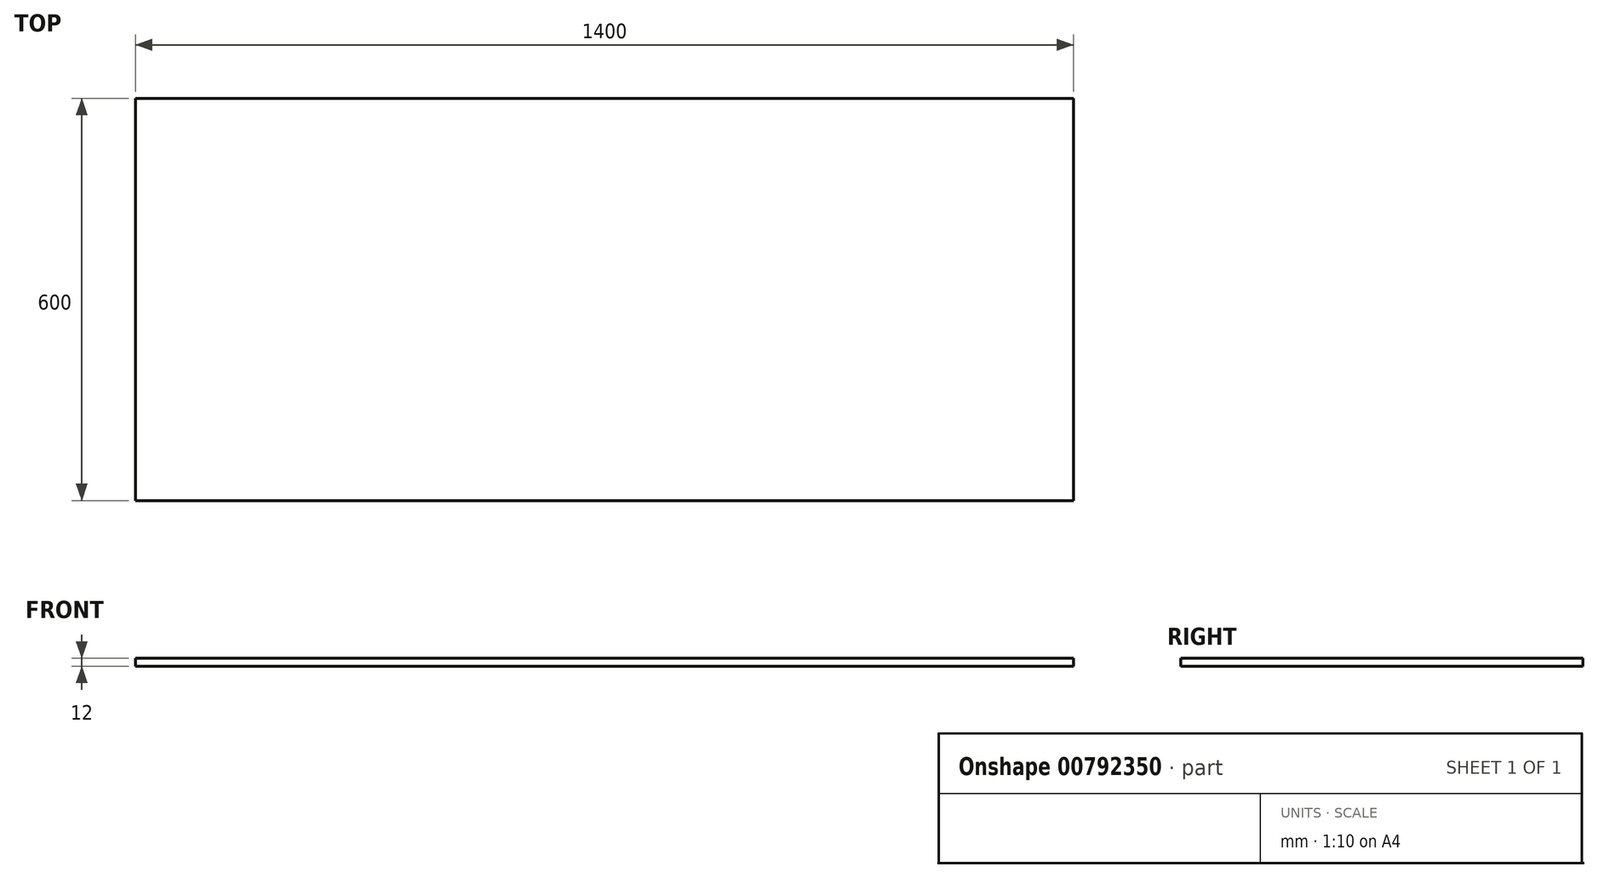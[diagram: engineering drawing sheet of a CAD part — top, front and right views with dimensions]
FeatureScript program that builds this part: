
annotation { "Feature Type Name" : "Feature", "Feature Type Description" : "" }
export const myFeature = defineFeature(function(context is Context, id is Id, definition is map)
    precondition{}
    {
        {
            var Q0;
            Q0=qCreatedBy(makeId("Top.planeOp"),FACE);
            var sketch = newSketch(context, id + "F0", { "sketchPlane" : qUnion([Q0])});
            skLineSegment(sketch, "E0.bottom", {"start": v(700, 300) * mm, "end": v(-700, 300) * mm});
            skLineSegment(sketch, "E0.top", {"start": v(700, -300) * mm, "end": v(-700, -300) * mm});
            skLineSegment(sketch, "E0.left", {"start": v(700, 300) * mm, "end": v(700, -300) * mm});
            skLineSegment(sketch, "E0.right", {"start": v(-700, 300) * mm, "end": v(-700, -300) * mm});
            skPoint(sketch, "E0.middle", {"position": v(0, 0) * mm});
            skSolve(sketch);
        }
        {
            var Q0;
            Q0 = qSketchRegion(id + "F0", true);
            extrude(context, id + "F1", {"entities" : qUnion([Q0]), "depth" : 12 * mm, "offsetDistance" : 25 * mm});
        }
    });
